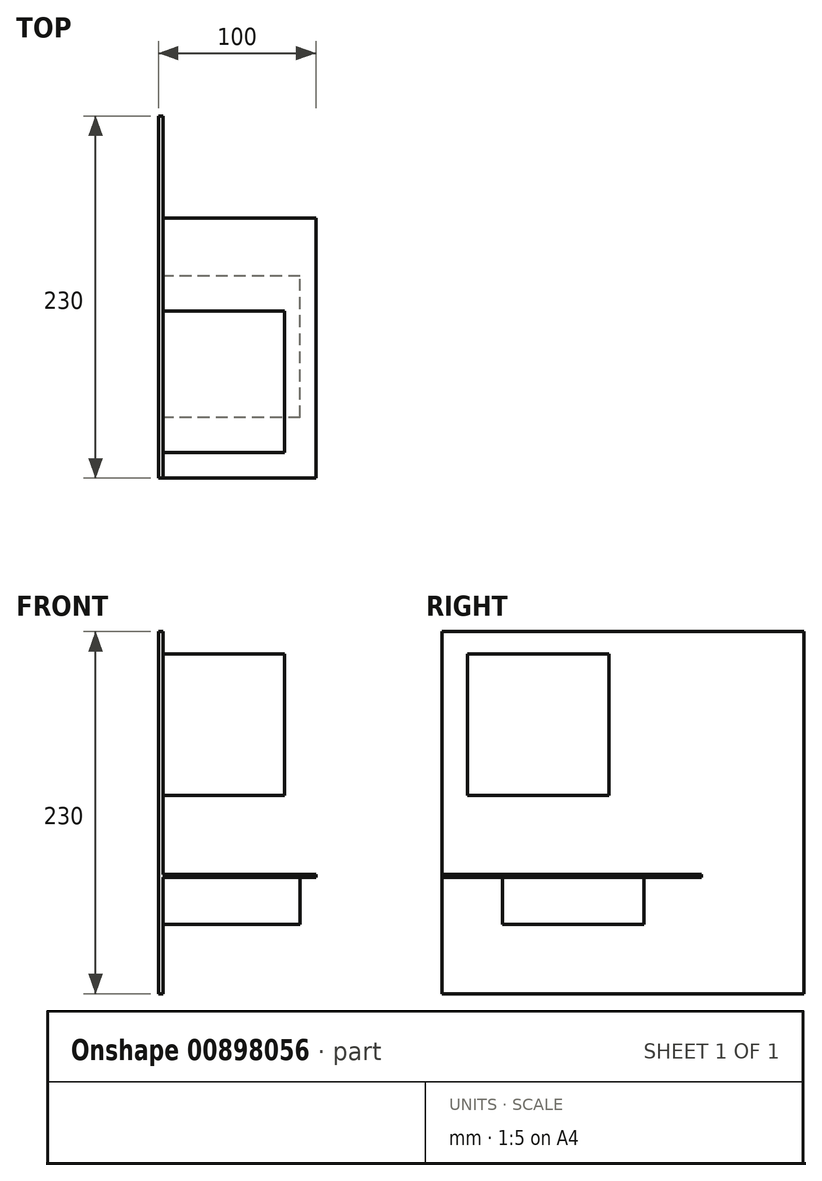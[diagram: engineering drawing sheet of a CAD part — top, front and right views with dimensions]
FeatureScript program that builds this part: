
annotation { "Feature Type Name" : "Feature", "Feature Type Description" : "" }
export const myFeature = defineFeature(function(context is Context, id is Id, definition is map)
    precondition{}
    {
        {
            var Q0;
            Q0=qCreatedBy(makeId("Right.planeOp"),FACE);
            var sketch = newSketch(context, id + "F0", { "sketchPlane" : qUnion([Q0])});
            skLineSegment(sketch, "E0.bottom", {"start": v(34.89, 154.68) * mm, "end": v(264.89, 154.68) * mm});
            skLineSegment(sketch, "E0.top", {"start": v(34.89, -75.32) * mm, "end": v(264.89, -75.32) * mm});
            skLineSegment(sketch, "E0.left", {"start": v(34.89, 154.68) * mm, "end": v(34.89, -75.32) * mm});
            skLineSegment(sketch, "E0.right", {"start": v(264.89, 154.68) * mm, "end": v(264.89, -75.32) * mm});
            skLineSegment(sketch, "E1.bottom", {"start": v(34.88, 0.54) * mm, "end": v(199.88, 0.54) * mm});
            skLineSegment(sketch, "E1.top", {"start": v(34.88, -1.46) * mm, "end": v(199.88, -1.46) * mm});
            skLineSegment(sketch, "E1.left", {"start": v(34.88, 0.54) * mm, "end": v(34.88, -1.46) * mm});
            skLineSegment(sketch, "E1.right", {"start": v(199.88, 0.54) * mm, "end": v(199.88, -1.46) * mm});
            skLineSegment(sketch, "E2.bottom", {"start": v(73.33, -1.46) * mm, "end": v(163.33, -1.46) * mm});
            skLineSegment(sketch, "E2.top", {"start": v(73.33, -31.46) * mm, "end": v(163.33, -31.46) * mm});
            skLineSegment(sketch, "E2.left", {"start": v(73.33, -1.46) * mm, "end": v(73.33, -31.46) * mm});
            skLineSegment(sketch, "E2.right", {"start": v(163.33, -1.46) * mm, "end": v(163.33, -31.46) * mm});
            skLineSegment(sketch, "E3.bottom", {"start": v(51.11, 50.54) * mm, "end": v(141.11, 50.54) * mm});
            skLineSegment(sketch, "E3.top", {"start": v(51.11, 140.54) * mm, "end": v(141.11, 140.54) * mm});
            skLineSegment(sketch, "E3.left", {"start": v(51.11, 50.54) * mm, "end": v(51.11, 140.54) * mm});
            skLineSegment(sketch, "E3.right", {"start": v(141.11, 50.54) * mm, "end": v(141.11, 140.54) * mm});
            skSolve(sketch);
        }
        {
            var Q0;
            {var subQ8=sQuery(id+"F0.wireOp",EDGE,"E0.bottom");Q0=makeQuery(id+"F0.imprint","IMPRINT",FACE,{"disambiguationData":[TD([[makeQuery(id+"F0.imprint","IMPRINT",EDGE,{"derivedFrom":subQ8}),-1.0]])]});}
            extrude(context, id + "F1", {"entities" : qUnion([Q0]), "depth" : 3 * mm, "offsetDistance" : 25.4 * mm});
        }
        {
            var Q0;
            Q0=makeQuery(id+"F0.imprint","IMPRINT",FACE,{"disambiguationData":[TD([[makeQuery(id+"F0.imprint","IMPRINT",EDGE,{"derivedFrom":sQuery(id+"F0.wireOp",EDGE,"E2.top")}),1.0]])]});
            extrude(context, id + "F2", {"entities" : qUnion([Q0]), "operationType" : NewBodyOperationType.ADD, "depth" : 90 * mm, "offsetDistance" : 25.4 * mm});
        }
        {
            var Q0;
            {var subQ6=sQuery(id+"F0.wireOp",EDGE,"E1.right");Q0=makeQuery(id+"F0.imprint","IMPRINT",FACE,{"disambiguationData":[TD([[makeQuery(id+"F0.imprint","IMPRINT",EDGE,{"derivedFrom":subQ6}),-1.0]])]});}
            extrude(context, id + "F3", {"entities" : qUnion([Q0]), "operationType" : NewBodyOperationType.ADD, "depth" : 100 * mm, "offsetDistance" : 25.4 * mm});
        }
        {
            var Q0;
            Q0=makeQuery(id+"F0.imprint","IMPRINT",FACE,{"disambiguationData":[TD([[makeQuery(id+"F0.imprint","IMPRINT",EDGE,{"derivedFrom":sQuery(id+"F0.wireOp",EDGE,"E3.bottom")}),1.0]])]});
            extrude(context, id + "F4", {"entities" : qUnion([Q0]), "operationType" : NewBodyOperationType.ADD, "depth" : 80 * mm, "offsetDistance" : 25 * mm});
        }
    });
